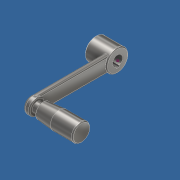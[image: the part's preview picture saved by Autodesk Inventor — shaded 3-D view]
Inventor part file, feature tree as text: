
AUTODESK INVENTOR PART (.ipt)
format: ipt  version: 2018 (Build 220112000, 112)  size: 219,648 bytes
history: native  units: mm
features: sketch x2, extrude x1, other x1
ambient origin geometry x8: Origin, YZ Plane, XZ Plane, XY Plane, X Axis, Y Axis, Z Axis, Center Point
bodies: Solid1 (feature_tree)
feature tree (4):
  extrude  "Extrusion1"  Depth=1.4mm
  sketch  "Sketch2"  dims[d4=3.4mm d5=0.0mm d6=0.0mm d7=1.5mm]
  sketch  "Sketch1"  dims[d1=3.0mm d3=1.4mm]
  other  "_Stainless Steel-Cranked handle GN 269-80-B10"
